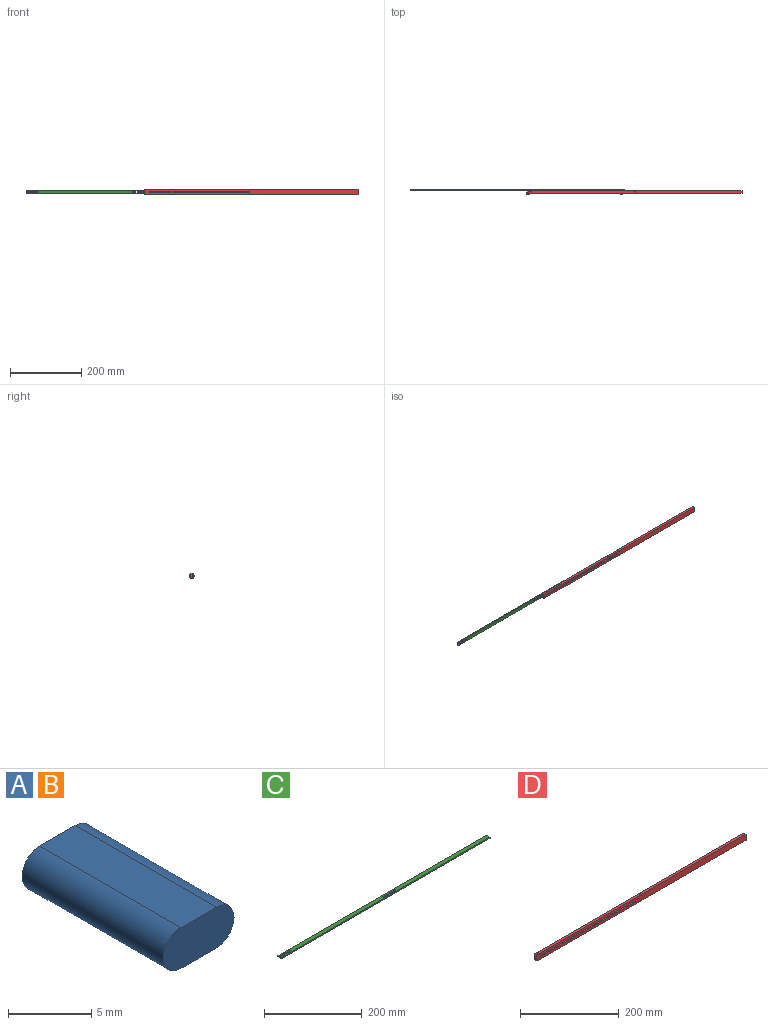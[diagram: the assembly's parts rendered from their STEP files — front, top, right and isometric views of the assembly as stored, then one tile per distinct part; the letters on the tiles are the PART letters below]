
ASSEMBLY  parts=4 mates=3
PART A: 6 faces, bbox 6x12x3 mm
  f0: plane 12x3mm, normal (0,0,-1), area 36mm2, adj f1,f3,f4,f5
  f1: cylinder r=1.5mm len=12mm, axis (0,1,0), area 56.5mm2, adj f0,f2,f4,f5
  f2: plane 12x3mm, normal (0,0,1), area 36mm2, adj f1,f3,f4,f5
  f3: cylinder r=1.5mm len=12mm, axis (0,1,0), area 56.5mm2, adj f0,f2,f4,f5
  f4: plane 6x3mm, normal (0,-1,0), area 16.1mm2, adj f0,f1,f2,f3
  f5: plane 6x3mm, normal (0,1,0), area 16.1mm2, adj f0,f1,f2,f3
PART B: same geometry as A
PART C: 14 faces, bbox 603x10x3 mm
  f0: cylinder r=1.5mm len=3mm, axis (0,0,1), area 14.3mm2, adj f1,f11,f12,f13
  f1: plane 30x3mm, normal (0,1,0), area 90mm2, adj f0,f2,f12,f13
  f2: plane 3.5x3mm, normal (-1,0,0), area 10.5mm2, adj f1,f3,f12,f13
  f3: plane 603x3mm, normal (0,-1,0), area 1809mm2, adj f2,f4,f12,f13
  f4: plane 10x3mm, normal (1,0,0), area 30mm2, adj f3,f5,f12,f13
  f5: plane 603x3mm, normal (0,1,0), area 1809mm2, adj f4,f6,f12,f13
  f6: plane 3.5x3mm, normal (-1,0,0), area 10.5mm2, adj f5,f11,f12,f13
  f7: plane 33x3mm, normal (0,-1,0), area 99mm2, adj f8,f10,f12,f13
  f8: cylinder r=1.5mm len=3mm, axis (0,0,1), area 14.1mm2, adj f7,f9,f12,f13
  f9: plane 33x3mm, normal (0,1,0), area 99mm2, adj f8,f10,f12,f13
  f10: cylinder r=1.5mm len=3mm, axis (0,0,1), area 14.1mm2, adj f7,f9,f12,f13
  f11: plane 29.94x3mm, normal (0,-1,0), area 89.8mm2, adj f0,f6,f12,f13
  f12: plane 603x10mm, normal (0,0,-1), area 5830.4mm2, adj f0,f1,f2,f3,f4,f5,f6,f7
  f13: plane 603x10mm, normal (0,0,1), area 5830.4mm2, adj f0,f1,f2,f3,f4,f5,f6,f7
PART D: 22 faces, bbox 600x6x15 mm
  f0: plane 277.5x6mm, normal (0,0,-1), area 1665mm2, adj f1,f19,f20,f21
  f1: cylinder r=1.5mm len=6mm, axis (0,1,0), area 28.3mm2, adj f0,f2,f20,f21
  f2: plane 277.5x6mm, normal (0,0,1), area 1665mm2, adj f1,f19,f20,f21
  f3: plane 6x3mm, normal (0,0,1), area 18mm2, adj f4,f18,f20,f21
  f4: cylinder r=3mm len=6mm, axis (0,1,0), area 28.3mm2, adj f3,f5,f20,f21
  f5: plane 6x3mm, normal (-1,0,0), area 18mm2, adj f4,f6,f20,f21
  f6: cylinder r=1.5mm len=6mm, axis (0,1,0), area 28.3mm2, adj f5,f7,f20,f21
  f7: plane 6x3mm, normal (-1,0,0), area 18mm2, adj f6,f8,f20,f21
  f8: cylinder r=3mm len=6mm, axis (0,1,0), area 28.3mm2, adj f7,f9,f20,f21
  f9: plane 6x3mm, normal (0,0,-1), area 18mm2, adj f8,f10,f20,f21
  f10: cylinder r=1.5mm len=6mm, axis (0,1,0), area 28.3mm2, adj f9,f11,f20,f21
  f11: plane 289.5x6mm, normal (0,0,-1), area 1737mm2, adj f10,f12,f20,f21
  f12: cylinder r=1.5mm len=6mm, axis (0,1,0), area 28.3mm2, adj f11,f13,f20,f21
  f13: plane 298.5x6mm, normal (0,0,-1), area 1791mm2, adj f12,f14,f20,f21
  f14: plane 15x6mm, normal (1,0,0), area 90mm2, adj f13,f15,f20,f21
  f15: plane 298.5x6mm, normal (0,0,1), area 1791mm2, adj f14,f16,f20,f21
  f16: cylinder r=1.5mm len=6mm, axis (0,1,0), area 28.3mm2, adj f15,f17,f20,f21
  f17: plane 289.5x6mm, normal (0,0,1), area 1737mm2, adj f16,f18,f20,f21
  f18: cylinder r=1.5mm len=6mm, axis (0,1,0), area 28.3mm2, adj f3,f17,f20,f21
  f19: cylinder r=1.5mm len=6mm, axis (0,1,0), area 28.3mm2, adj f0,f2,f20,f21
  f20: plane 600x15mm, normal (0,-1,0), area 8138.9mm2, adj f0,f1,f2,f3,f4,f5,f6,f7
  f21: plane 600x15mm, normal (0,1,0), area 8138.9mm2, adj f0,f1,f2,f3,f4,f5,f6,f7
PLACE A t=(-27.07,-9.35,0.38)mm
PLACE B t=(-289.57,-9.35,0.38)mm
PLACE C rot(axis=(-1,0,0),90deg) t=(-377.35,-3.35,47.24)mm
PLACE D t=(-250.77,-9.35,45.74)mm
MATE pin_slot B.f1 <-> D.f6  axis (0,1,0) through (-377.35,-9.35,47.24)mm
MATE pin_slot C.f8 <-> B.f1  axis (0,1,0) through (-377.35,-3.35,47.24)mm
MATE pin_slot A.f1 <-> D.f1  axis (0,1,0) through (-114.85,-9.35,47.24)mm
